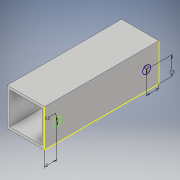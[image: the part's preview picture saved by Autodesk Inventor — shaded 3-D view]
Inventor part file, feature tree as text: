
AUTODESK INVENTOR PART (.ipt)
format: ipt  version: 2019 (Build 230136000, 136)  size: 112,640 bytes
history: native  units: mm
features: sketch x2, other x1, extrude x1
ambient origin geometry x8: Origin, YZ Plane, XZ Plane, XY Plane, X Axis, Y Axis, Z Axis, Center Point
bodies: Body1 (feature_tree)
feature tree (4):
  other  "ソリッド1"
  extrude  "押し出し1"  Depth=15.0mm
  sketch  "スケッチ2"
  sketch  "スケッチ1"
